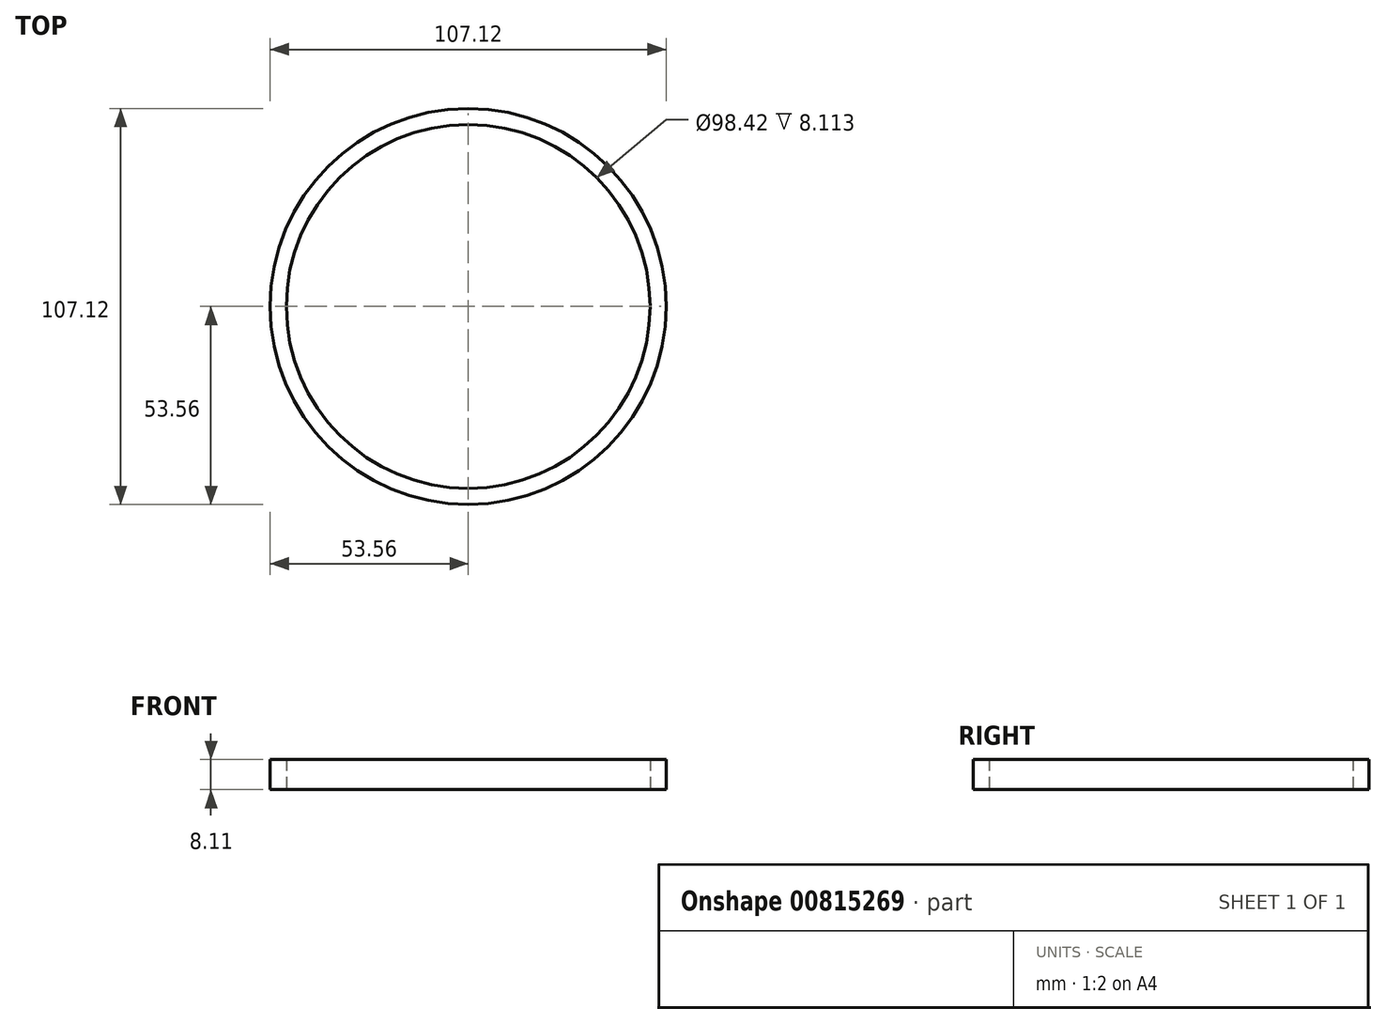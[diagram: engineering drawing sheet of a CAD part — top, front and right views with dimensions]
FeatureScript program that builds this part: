
annotation { "Feature Type Name" : "Feature", "Feature Type Description" : "" }
export const myFeature = defineFeature(function(context is Context, id is Id, definition is map)
    precondition{}
    {
        {
            var Q0;
            Q0=qCreatedBy(makeId("Top.planeOp"),FACE);
            var sketch = newSketch(context, id + "F0", { "sketchPlane" : qUnion([Q0])});
            skCircle(sketch, "E0", {"center": v(0, 0) * mm, "radius": 49.21 * mm});
            skCircle(sketch, "E1", {"center": v(0, 0) * mm, "radius": 53.56 * mm});
            skSolve(sketch);
        }
        {
            var Q0;
            Q0=makeQuery(id+"F0.imprint","IMPRINT",FACE,{"disambiguationData":[TD([[makeQuery(id+"F0.imprint","IMPRINT",EDGE,{"derivedFrom":sQuery(id+"F0.wireOp",EDGE,"E0")}),-1.0]])]});
            extrude(context, id + "F1", {"entities" : qUnion([Q0]), "depth" : 11.1 * mm - 3 * mm, "offsetDistance" : 25.4 * mm});
        }
    });
